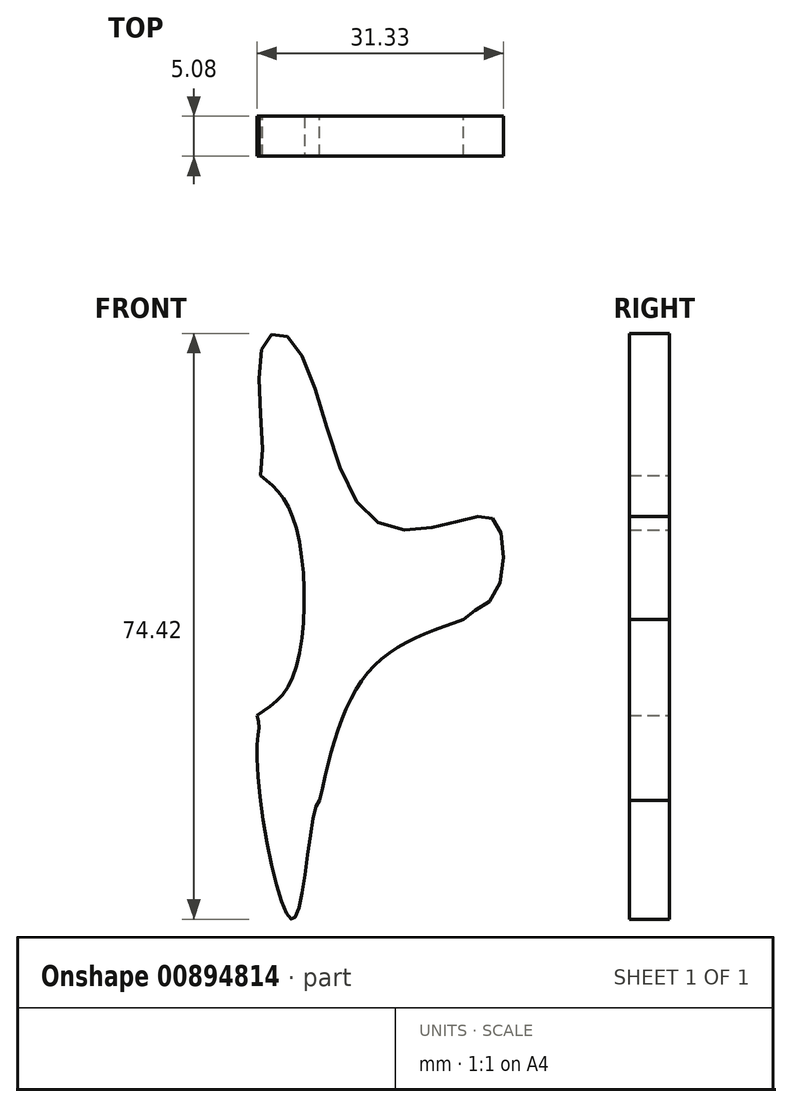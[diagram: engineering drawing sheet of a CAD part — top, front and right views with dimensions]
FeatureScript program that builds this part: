
annotation { "Feature Type Name" : "Feature", "Feature Type Description" : "" }
export const myFeature = defineFeature(function(context is Context, id is Id, definition is map)
    precondition{}
    {
        {
            var Q0;
            Q0=qCreatedBy(makeId("Front.planeOp"),FACE);
            var sketch = newSketch(context, id + "F0", { "sketchPlane" : qUnion([Q0])});
            skFitSpline(sketch, "E0", {"points": [v(-9.55, -104.84) * mm, v(-13.3, -104.84) * mm, v(-13.77, -121.73) * mm, v(-17.06, -125.49) * mm, v(-20.34, -142.38) * mm, v(-14.24, -152.24) * mm, v(-14.24, -157.4) * mm, v(-9.55, -178.04) * mm, v(-6.26, -163.03) * mm, v(0, -174.76) * mm, v(12.04, -156.93) * mm, v(12.04, -140.03) * mm, v(15.8, -137.22) * mm, v(16.26, -127.83) * mm, v(12.04, -127.36) * mm, v(0, -126.9) * mm, v(-9.55, -104.84) * mm]});
            skFitSpline(sketch, "E1", {"points": [v(-6.26, -163.03) * mm, v(0, -146.6) * mm, v(12.04, -140.03) * mm], "startDerivative": vector(8.11, 35.42) * mm, "endDerivative": vector(28.92, 10.04) * mm});
            skFitSpline(sketch, "E2", {"points": [v(-14.24, -152.24) * mm, v(-9.55, -147.07) * mm, v(-9.55, -127.36) * mm, v(-13.77, -121.73) * mm], "startDerivative": vector(19.87, 12.56) * mm, "endDerivative": vector(-17.58, 14.4) * mm});
            skSolve(sketch);
        }
        {
            var Q0;
            {var subQ0=sQuery(id+"F0.wireOp",EDGE,"E1");Q0=makeQuery(id+"F0.imprint","IMPRINT",FACE,{"disambiguationData":[TD([[makeQuery(id+"F0.imprint","IMPRINT",EDGE,{"derivedFrom":subQ0}),1.0]])]});}
            extrude(context, id + "F1", {"entities" : qUnion([Q0]), "depth" : 2.54 * mm, "offsetDistance" : 25.4 * mm});
        }
        {
            var Q0;
            Q0=makeQuery(id+"F1.opExtrude","CAP_FACE",FACE,{"disambiguationData":[OSD([sQuery(id+"F0.wireOp",EDGE,"E0"),sQuery(id+"F0.wireOp",EDGE,"E1"),sQuery(id+"F0.wireOp",EDGE,"E2")])],"isStart":true});
            extrude(context, id + "F2", {"entities" : qUnion([Q0]), "operationType" : NewBodyOperationType.ADD, "depth" : 2.54 * mm, "offsetDistance" : 25.4 * mm});
        }
        {
            var Q0;
            {var subQ0=sQuery(id+"F0.wireOp",EDGE,"E2");Q0=makeQuery(id+"F0.imprint","IMPRINT",FACE,{"disambiguationData":[TD([[makeQuery(id+"F0.imprint","IMPRINT",EDGE,{"derivedFrom":subQ0}),1.0]])]});}
            var Q1;
            {var subQ0=sQuery(id+"F0.wireOp",EDGE,"E1");Q1=makeQuery(id+"F0.imprint","IMPRINT",FACE,{"disambiguationData":[TD([[makeQuery(id+"F0.imprint","IMPRINT",EDGE,{"derivedFrom":subQ0}),-1.0]])]});}
            extrude(context, id + "F3", {"entities" : qUnion([Q0, Q1]), "operationType" : NewBodyOperationType.ADD, "depth" : 2.54 * mm, "offsetDistance" : 25.4 * mm});
        }
        {
            var Q0;
            {var subQ0=sQuery(id+"F0.wireOp",EDGE,"E1");Q0=makeQuery(id+"F0.imprint","IMPRINT",FACE,{"disambiguationData":[TD([[makeQuery(id+"F0.imprint","IMPRINT",EDGE,{"derivedFrom":subQ0}),-1.0]])]});}
            var Q1;
            {var subQ0=sQuery(id+"F0.wireOp",EDGE,"E2");Q1=makeQuery(id+"F0.imprint","IMPRINT",FACE,{"disambiguationData":[TD([[makeQuery(id+"F0.imprint","IMPRINT",EDGE,{"derivedFrom":subQ0}),1.0]])]});}
            extrude(context, id + "F4", {"entities" : qUnion([Q0, Q1]), "operationType" : NewBodyOperationType.REMOVE, "depth" : 2.54 * mm, "offsetDistance" : 25.4 * mm});
        }
    });
